# Revit family: AISC Tube Shapes-Section
name_source: partatom
category: Detail Items
revit_build: Autodesk Revit Architecture 2012 (Build: 20110210_1515)
units: mm (PartAtom-declared; Revit-internal decimal feet)

## types (374) — shared parameters
Keynote = 05 12 00.L0

## per-type parameters (varying)
| type | A | Ht | Shape | W | b | r | t |
| HSS20X12X5/8 | 0.24 SF | 1' - 8" | Rect. | 127 | 1' - 0" | 0' - 1 5/32" | 0' - 0 19/32" |
| HSS20X12X1/2 | 0.2 SF | 1' - 8" | Rect. | 103 | 1' - 0" | 0' - 0 15/16" | 0' - 0 15/32" |
| HSS20X12X3/8 | 0.15 SF | 1' - 8" | Rect. | 78.4 | 1' - 0" | 0' - 0 11/16" | 0' - 0 11/32" |
| HSS20X12X5/16 | 0.13 SF | 1' - 8" | Rect. | 65.8 | 1' - 0" | 0' - 0 19/32" | 0' - 0 9/32" |
| HSS20X8X5/8 | 0.21 SF | 1' - 8" | Rect. | 110 | 0' - 8" | 0' - 1 5/32" | 0' - 0 19/32" |
| HSS20X8X1/2 | 0.17 SF | 1' - 8" | Rect. | 89.6 | 0' - 8" | 0' - 0 15/16" | 0' - 0 15/32" |
| HSS20X8X3/8 | 0.13 SF | 1' - 8" | Rect. | 68.3 | 0' - 8" | 0' - 0 11/16" | 0' - 0 11/32" |
| HSS20X8X5/16 | 0.11 SF | 1' - 8" | Rect. | 57.3 | 0' - 8" | 0' - 0 19/32" | 0' - 0 9/32" |
| HSS20X4X1/2 | 0.15 SF | 1' - 8" | Rect. | 75.9 | 0' - 4" | 0' - 0 15/16" | 0' - 0 15/32" |
| HSS20X4X3/8 | 0.11 SF | 1' - 8" | Rect. | 58.1 | 0' - 4" | 0' - 0 11/16" | 0' - 0 11/32" |
| HSS20X4X5/16 | 0.09 SF | 1' - 8" | Rect. | 48.9 | 0' - 4" | 0' - 0 19/32" | 0' - 0 9/32" |
| HSS20X4X1/4 | 0.08 SF | 1' - 8" | Rect. | 39.5 | 0' - 4" | 0' - 0 15/32" | 0' - 0 7/32" |
| HSS18X12X5/8 - Obsolete | 0.23 SF | 1' - 6" | Rect. | 119 | 1' - 0" | 0' - 1 5/32" | 0' - 0 19/32" |
| HSS18X12X1/2 - Obsolete | 0.18 SF | 1' - 6" | Rect. | 96.4 | 1' - 0" | 0' - 0 15/16" | 0' - 0 15/32" |
| HSS18X12X3/8 - Obsolete | 0.14 SF | 1' - 6" | Rect. | 73.3 | 1' - 0" | 0' - 0 11/16" | 0' - 0 11/32" |
| HSS18X6X5/8 | 0.18 SF | 1' - 6" | Rect. | 93.1 | 0' - 6" | 0' - 1 5/32" | 0' - 0 19/32" |
| HSS18X6X1/2 | 0.15 SF | 1' - 6" | Rect. | 75.9 | 0' - 6" | 0' - 0 15/16" | 0' - 0 15/32" |
| HSS18X6X3/8 | 0.11 SF | 1' - 6" | Rect. | 58.1 | 0' - 6" | 0' - 0 11/16" | 0' - 0 11/32" |
| HSS18X6X5/16 | 0.09 SF | 1' - 6" | Rect. | 48.9 | 0' - 6" | 0' - 0 19/32" | 0' - 0 9/32" |
| HSS18X6X1/4 | 0.08 SF | 1' - 6" | Rect. | 39.5 | 0' - 6" | 0' - 0 15/32" | 0' - 0 7/32" |
| HSS16X16X5/8 | 0.24 SF | 1' - 4" | Square | 127 | 1' - 4" | 0' - 1 5/32" | 0' - 0 19/32" |
| HSS16X16X1/2 | 0.2 SF | 1' - 4" | Square | 103 | 1' - 4" | 0' - 0 15/16" | 0' - 0 15/32" |
| HSS16X16X3/8 | 0.15 SF | 1' - 4" | Square | 78.4 | 1' - 4" | 0' - 0 11/16" | 0' - 0 11/32" |
| HSS16X16X5/16 | 0.13 SF | 1' - 4" | Square | 65.8 | 1' - 4" | 0' - 0 19/32" | 0' - 0 9/32" |
| HSS16X12X5/8 | 0.21 SF | 1' - 4" | Rect. | 110 | 1' - 0" | 0' - 1 5/32" | 0' - 0 19/32" |
| HSS16X12X1/2 | 0.17 SF | 1' - 4" | Rect. | 89.6 | 1' - 0" | 0' - 0 15/16" | 0' - 0 15/32" |
| HSS16X12X3/8 | 0.13 SF | 1' - 4" | Rect. | 68.3 | 1' - 0" | 0' - 0 11/16" | 0' - 0 11/32" |
| HSS16X12X5/16 | 0.11 SF | 1' - 4" | Rect. | 57.4 | 1' - 0" | 0' - 0 19/32" | 0' - 0 9/32" |
| HSS16X8X5/8 | 0.18 SF | 1' - 4" | Rect. | 93.1 | 0' - 8" | 0' - 1 5/32" | 0' - 0 19/32" |
| HSS16X8X1/2 | 0.15 SF | 1' - 4" | Rect. | 75.9 | 0' - 8" | 0' - 0 15/16" | 0' - 0 15/32" |
| HSS16X8X3/8 | 0.11 SF | 1' - 4" | Rect. | 58.1 | 0' - 8" | 0' - 0 11/16" | 0' - 0 11/32" |
| HSS16X8X5/16 | 0.09 SF | 1' - 4" | Rect. | 48.9 | 0' - 8" | 0' - 0 19/32" | 0' - 0 9/32" |
| HSS16X8X1/4 | 0.08 SF | 1' - 4" | Rect. | 39.5 | 0' - 8" | 0' - 0 15/32" | 0' - 0 7/32" |
| HSS16X4X5/8 | 0.15 SF | 1' - 4" | Rect. | 76.1 | 0' - 4" | 0' - 1 5/32" | 0' - 0 19/32" |
| HSS16X4X1/2 | 0.12 SF | 1' - 4" | Rect. | 62.3 | 0' - 4" | 0' - 0 15/16" | 0' - 0 15/32" |
| HSS16X4X3/8 | 0.09 SF | 1' - 4" | Rect. | 47.9 | 0' - 4" | 0' - 0 11/16" | 0' - 0 11/32" |
| HSS16X4X5/16 | 0.08 SF | 1' - 4" | Rect. | 40.3 | 0' - 4" | 0' - 0 19/32" | 0' - 0 9/32" |
| HSS16X4X1/4 | 0.06 SF | 1' - 4" | Rect. | 32.7 | 0' - 4" | 0' - 0 15/32" | 0' - 0 7/32" |
| HSS16X4X3/16 | 0.05 SF | 1' - 2" | Rect. | 24.7 | 0' - 4" | 0' - 0 11/32" | 0' - 0 3/16" |
| HSS14X14X5/8 | 0.21 SF | 1' - 2" | Square | 110 | 1' - 2" | 0' - 1 5/32" | 0' - 0 19/32" |
| HSS14X14X1/2 | 0.17 SF | 1' - 2" | Square | 89.6 | 1' - 2" | 0' - 0 15/16" | 0' - 0 15/32" |
| HSS14X14X3/8 | 0.13 SF | 1' - 2" | Square | 68.2 | 1' - 2" | 0' - 0 11/16" | 0' - 0 11/32" |
| HSS14X14X5/16 | 0.11 SF | 1' - 2" | Square | 57.3 | 1' - 2" | 0' - 0 19/32" | 0' - 0 9/32" |
| HSS14X12X1/2 - Obsolete | 0.16 SF | 1' - 2" | Rect. | 82.7 | 1' - 0" | 0' - 0 15/16" | 0' - 0 15/32" |
| HSS14X12X3/8 - Obsolete | 0.12 SF | 1' - 2" | Rect. | 63.1 | 1' - 0" | 0' - 0 11/16" | 0' - 0 11/32" |
| HSS14X10X5/8 | 0.18 SF | 1' - 2" | Rect. | 93.1 | 0' - 10" | 0' - 1 5/32" | 0' - 0 19/32" |
| HSS14X10X1/2 | 0.15 SF | 1' - 2" | Rect. | 75.9 | 0' - 10" | 0' - 0 15/16" | 0' - 0 15/32" |
| HSS14X10X3/8 | 0.11 SF | 1' - 2" | Rect. | 58.1 | 0' - 10" | 0' - 0 11/16" | 0' - 0 11/32" |
| HSS14X10X5/16 | 0.09 SF | 1' - 2" | Rect. | 48.9 | 0' - 10" | 0' - 0 19/32" | 0' - 0 9/32" |
| HSS14X10X1/4 | 0.08 SF | 1' - 2" | Rect. | 39.5 | 0' - 10" | 0' - 0 15/32" | 0' - 0 7/32" |
| HSS14X6X5/8 | 0.15 SF | 1' - 2" | Rect. | 76.1 | 0' - 10" | 0' - 1 5/32" | 0' - 0 19/32" |
| HSS14X6X1/2 | 0.12 SF | 1' - 2" | Rect. | 62.3 | 0' - 6" | 0' - 0 15/16" | 0' - 0 15/32" |
| HSS14X6X3/8 | 0.09 SF | 1' - 2" | Rect. | 47.9 | 0' - 6" | 0' - 0 11/16" | 0' - 0 11/32" |
| HSS14X6X5/16 | 0.08 SF | 1' - 2" | Rect. | 40.3 | 0' - 6" | 0' - 0 19/32" | 0' - 0 9/32" |
| HSS14X6X1/4 | 0.06 SF | 1' - 2" | Rect. | 32.7 | 0' - 6" | 0' - 0 15/32" | 0' - 0 7/32" |
| HSS14X6X3/16 | 0.05 SF | 1' - 2" | Rect. | 24.7 | 0' - 6" | 0' - 0 11/32" | 0' - 0 3/16" |
| HSS14X4X5/8 | 0.13 SF | 1' - 2" | Rect. | 67.6 | 0' - 4" | 0' - 1 5/32" | 0' - 0 19/32" |
| HSS14X4X1/2 | 0.11 SF | 1' - 2" | Rect. | 55.5 | 0' - 4" | 0' - 0 15/16" | 0' - 0 15/32" |
| HSS14X4X3/8 | 0.08 SF | 1' - 2" | Rect. | 42.7 | 0' - 4" | 0' - 0 11/16" | 0' - 0 11/32" |
| HSS14X4X5/16 | 0.07 SF | 1' - 2" | Rect. | 36.1 | 0' - 4" | 0' - 0 19/32" | 0' - 0 9/32" |
| HSS14X4X1/4 | 0.06 SF | 1' - 2" | Rect. | 29.2 | 0' - 4" | 0' - 0 15/32" | 0' - 0 7/32" |
| HSS14X4X3/16 | 0.04 SF | 1' - 2" | Rect. | 22.1 | 0' - 4" | 0' - 0 11/32" | 0' - 0 3/16" |
| HSS12X12X5/8 | 0.18 SF | 1' - 0" | Square | 93.1 | 1' - 0" | 0' - 1 5/32" | 0' - 0 19/32" |
| HSS12X12X1/2 | 0.15 SF | 1' - 0" | Square | 75.9 | 1' - 0" | 0' - 0 15/16" | 0' - 0 15/32" |
| HSS12X12X3/8 | 0.11 SF | 1' - 0" | Square | 58 | 1' - 0" | 0' - 0 11/16" | 0' - 0 11/32" |
| HSS12X12X5/16 | 0.09 SF | 1' - 0" | Square | 48.8 | 1' - 0" | 0' - 0 19/32" | 0' - 0 9/32" |
| HSS12X12X1/4 | 0.08 SF | 1' - 0" | Square | 39.4 | 1' - 0" | 0' - 0 15/32" | 0' - 0 7/32" |
| HSS12X12X3/16 | 0.06 SF | 1' - 0" | Square | 29.8 | 1' - 0" | 0' - 0 11/32" | 0' - 0 3/16" |
| HSS12X10X1/2 | 0.13 SF | 1' - 0" | Rect. | 69.1 | 0' - 10" | 0' - 0 15/16" | 0' - 0 15/32" |
| HSS12X10X3/8 | 0.1 SF | 1' - 0" | Rect. | 52.9 | 0' - 10" | 0' - 0 11/16" | 0' - 0 11/32" |
| HSS12X10X5/16 | 0.08 SF | 1' - 0" | Rect. | 44.6 | 0' - 10" | 0' - 0 19/32" | 0' - 0 9/32" |
| HSS12X10X1/4 | 0.07 SF | 1' - 0" | Rect. | 36 | 0' - 10" | 0' - 0 15/32" | 0' - 0 7/32" |
| HSS12X8X5/8 | 0.15 SF | 1' - 0" | Rect. | 76.1 | 0' - 8" | 0' - 1 5/32" | 0' - 0 19/32" |
| HSS12X8X1/2 | 0.12 SF | 1' - 0" | Rect. | 62.3 | 0' - 8" | 0' - 0 15/16" | 0' - 0 15/32" |
| HSS12X8X3/8 | 0.09 SF | 1' - 0" | Rect. | 47.8 | 0' - 8" | 0' - 0 11/16" | 0' - 0 11/32" |
| HSS12X8X5/16 | 0.08 SF | 1' - 0" | Rect. | 40.4 | 0' - 8" | 0' - 0 19/32" | 0' - 0 9/32" |
| HSS12X8X1/4 | 0.06 SF | 1' - 0" | Rect. | 32.6 | 0' - 8" | 0' - 0 15/32" | 0' - 0 7/32" |
| HSS12X8X3/16 | 0.05 SF | 1' - 0" | Rect. | 24.8 | 0' - 8" | 0' - 0 11/32" | 0' - 0 3/16" |
| HSS12X6X5/8 | 0.13 SF | 1' - 0" | Rect. | 67.6 | 0' - 6" | 0' - 1 5/32" | 0' - 0 19/32" |
| HSS12X6X1/2 | 0.11 SF | 1' - 0" | Rect. | 55.5 | 0' - 6" | 0' - 0 15/16" | 0' - 0 15/32" |
| HSS12X6X3/8 | 0.08 SF | 1' - 0" | Rect. | 42.7 | 0' - 6" | 0' - 0 11/16" | 0' - 0 11/32" |
| HSS12X6X5/16 | 0.07 SF | 1' - 0" | Rect. | 36.1 | 0' - 6" | 0' - 0 19/32" | 0' - 0 9/32" |
| HSS12X6X1/4 | 0.06 SF | 1' - 0" | Rect. | 29.2 | 0' - 6" | 0' - 0 15/32" | 0' - 0 7/32" |
| HSS12X6X3/16 | 0.04 SF | 1' - 0" | Rect. | 22.2 | 0' - 6" | 0' - 0 11/32" | 0' - 0 3/16" |
| HSS12X4X5/8 | 0.11 SF | 1' - 0" | Rect. | 59.1 | 0' - 4" | 0' - 1 5/32" | 0' - 0 19/32" |
| HSS12X4X1/2 | 0.09 SF | 1' - 0" | Rect. | 48.7 | 0' - 4" | 0' - 0 15/16" | 0' - 0 15/32" |
| HSS12X4X3/8 | 0.07 SF | 1' - 0" | Rect. | 37.6 | 0' - 4" | 0' - 0 11/16" | 0' - 0 11/32" |
| HSS12X4X5/16 | 0.06 SF | 1' - 0" | Rect. | 31.8 | 0' - 4" | 0' - 0 19/32" | 0' - 0 9/32" |
| HSS12X4X1/4 | 0.05 SF | 1' - 0" | Rect. | 25.8 | 0' - 4" | 0' - 0 15/32" | 0' - 0 7/32" |
| HSS12X4X3/16 | 0.04 SF | 1' - 0" | Rect. | 19.7 | 0' - 4" | 0' - 0 11/32" | 0' - 0 3/16" |
| HSS12X3-1/2X3/8 | 0.07 SF | 1' - 0" | Rect. | 36.3 | 0' - 3 1/2" | 0' - 0 11/16" | 0' - 0 11/32" |
| HSS12X3-1/2X5/16 | 0.06 SF | 1' - 0" | Rect. | 30.8 | 0' - 3 1/2" | 0' - 0 19/32" | 0' - 0 9/32" |
| HSS12X3X5/16 | 0.06 SF | 1' - 0" | Rect. | 29.7 | 0' - 3" | 0' - 0 19/32" | 0' - 0 9/32" |
| HSS12X3X1/4 | 0.05 SF | 1' - 0" | Rect. | 24.1 | 0' - 3" | 0' - 0 15/32" | 0' - 0 7/32" |
| HSS12X3X3/16 | 0.03 SF | 1' - 0" | Rect. | 18.4 | 0' - 3" | 0' - 0 11/32" | 0' - 0 3/16" |
| HSS12X2X5/16 | 0.05 SF | 1' - 0" | Rect. | 27.6 | 0' - 2" | 0' - 0 19/32" | 0' - 0 9/32" |
| HSS12X2X1/4 | 0.04 SF | 1' - 0" | Rect. | 22.4 | 0' - 2" | 0' - 0 15/32" | 0' - 0 7/32" |
| HSS12X2X3/16 | 0.03 SF | 1' - 0" | Rect. | 17.1 | 0' - 2" | 0' - 0 11/32" | 0' - 0 3/16" |
| HSS10X10X5/8 | 0.15 SF | 0' - 10" | Square | 76.1 | 0' - 10" | 0' - 1 5/32" | 0' - 0 19/32" |
| HSS10X10X1/2 | 0.12 SF | 0' - 10" | Square | 62.3 | 0' - 10" | 0' - 0 15/16" | 0' - 0 15/32" |
| HSS10X10X3/8 | 0.09 SF | 0' - 10" | Square | 47.8 | 0' - 10" | 0' - 0 11/16" | 0' - 0 11/32" |
| HSS10X10X5/16 | 0.08 SF | 0' - 10" | Square | 40.3 | 0' - 10" | 0' - 0 19/32" | 0' - 0 9/32" |
| HSS10X10X1/4 | 0.06 SF | 0' - 10" | Square | 32.6 | 0' - 10" | 0' - 0 15/32" | 0' - 0 7/32" |
| HSS10X10X3/16 | 0.05 SF | 0' - 10" | Square | 24.7 | 0' - 10" | 0' - 0 11/32" | 0' - 0 3/16" |
| HSS10X8X5/8 | 0.13 SF | 0' - 10" | Rect. | 67.6 | 0' - 8" | 0' - 1 5/32" | 0' - 0 19/32" |
| HSS10X8X1/2 | 0.11 SF | 0' - 10" | Rect. | 55.5 | 0' - 8" | 0' - 0 15/16" | 0' - 0 15/32" |
| HSS10X8X3/8 | 0.08 SF | 0' - 10" | Rect. | 42.7 | 0' - 8" | 0' - 0 11/16" | 0' - 0 11/32" |
| HSS10X8X5/16 | 0.07 SF | 0' - 10" | Rect. | 36.1 | 0' - 8" | 0' - 0 19/32" | 0' - 0 9/32" |
| HSS10X8X1/4 | 0.06 SF | 0' - 10" | Rect. | 29.2 | 0' - 8" | 0' - 0 15/32" | 0' - 0 7/32" |
| HSS10X8X3/16 | 0.04 SF | 0' - 10" | Rect. | 22.2 | 0' - 8" | 0' - 0 11/32" | 0' - 0 3/16" |
| HSS10X6X5/8 | 0.11 SF | 0' - 10" | Rect. | 59.1 | 0' - 6" | 0' - 1 5/32" | 0' - 0 19/32" |
| HSS10X6X1/2 | 0.09 SF | 0' - 10" | Rect. | 48.7 | 0' - 6" | 0' - 0 15/16" | 0' - 0 15/32" |
| HSS10X6X3/8 | 0.07 SF | 0' - 10" | Rect. | 37.6 | 0' - 6" | 0' - 0 11/16" | 0' - 0 11/32" |
| HSS10X6X5/16 | 0.06 SF | 0' - 10" | Rect. | 31.8 | 0' - 6" | 0' - 0 19/32" | 0' - 0 9/32" |
| HSS10X6X1/4 | 0.05 SF | 0' - 10" | Rect. | 25.8 | 0' - 6" | 0' - 0 15/32" | 0' - 0 7/32" |
| HSS10X6X3/16 | 0.04 SF | 0' - 10" | Rect. | 19.7 | 0' - 6" | 0' - 0 11/32" | 0' - 0 3/16" |
| HSS10X5X3/8 | 0.07 SF | 0' - 10" | Rect. | 35.1 | 0' - 5" | 0' - 0 11/16" | 0' - 0 11/32" |
| HSS10X5X5/16 | 0.06 SF | 0' - 10" | Rect. | 29.7 | 0' - 5" | 0' - 0 19/32" | 0' - 0 9/32" |
| HSS10X5X1/4 | 0.05 SF | 0' - 10" | Rect. | 24.1 | 0' - 5" | 0' - 0 15/32" | 0' - 0 7/32" |
| HSS10X5X3/16 | 0.03 SF | 0' - 10" | Rect. | 18.4 | 0' - 5" | 0' - 0 11/32" | 0' - 0 3/16" |
| HSS10X4X5/8 | 0.1 SF | 0' - 10" | Rect. | 50.6 | 0' - 4" | 0' - 1 5/32" | 0' - 0 19/32" |
| HSS10X4X1/2 | 0.08 SF | 0' - 10" | Rect. | 41.9 | 0' - 4" | 0' - 0 15/16" | 0' - 0 15/32" |
| HSS10X4X3/8 | 0.06 SF | 0' - 10" | Rect. | 32.5 | 0' - 4" | 0' - 0 11/16" | 0' - 0 11/32" |
| HSS10X4X5/16 | 0.05 SF | 0' - 10" | Rect. | 27.6 | 0' - 4" | 0' - 0 19/32" | 0' - 0 9/32" |
| HSS10X4X1/4 | 0.04 SF | 0' - 10" | Rect. | 22.4 | 0' - 4" | 0' - 0 15/32" | 0' - 0 7/32" |
| HSS10X4X3/16 | 0.03 SF | 0' - 10" | Rect. | 17.1 | 0' - 4" | 0' - 0 11/32" | 0' - 0 3/16" |
| HSS10X4X1/8 | 0.02 SF | 0' - 10" | Rect. | 11.6 | 0' - 4" | 0' - 0 7/32" | 0' - 0 1/8" |
| HSS10X3-1/2X1/2 | 0.08 SF | 0' - 10" | Rect. | 40.2 | 0' - 3 1/2" | 0' - 0 15/16" | 0' - 0 15/32" |
| HSS10X3-1/2X3/8 | 0.06 SF | 0' - 10" | Rect. | 31.2 | 0' - 3 1/2" | 0' - 0 11/16" | 0' - 0 11/32" |
| HSS10X3-1/2X5/16 | 0.05 SF | 0' - 10" | Rect. | 26.5 | 0' - 3 1/2" | 0' - 0 19/32" | 0' - 0 9/32" |
| HSS10X3-1/2X1/4 | 0.04 SF | 0' - 10" | Rect. | 21.5 | 0' - 3 1/2" | 0' - 0 15/32" | 0' - 0 7/32" |
| HSS10X3-1/2X3/16 | 0.03 SF | 0' - 10" | Rect. | 16.5 | 0' - 3 1/2" | 0' - 0 11/32" | 0' - 0 3/16" |
| HSS10X3-1/2X1/8 | 0.02 SF | 0' - 10" | Rect. | 11.1 | 0' - 3 1/2" | 0' - 0 7/32" | 0' - 0 1/8" |
| HSS10X3X3/8 | 0.06 SF | 0' - 10" | Rect. | 30 | 0' - 3" | 0' - 0 11/16" | 0' - 0 11/32" |
| HSS10X3X5/16 | 0.05 SF | 0' - 10" | Rect. | 25.4 | 0' - 3" | 0' - 0 19/32" | 0' - 0 9/32" |
| HSS10X3X1/4 | 0.04 SF | 0' - 10" | Rect. | 20.7 | 0' - 3" | 0' - 0 15/32" | 0' - 0 7/32" |
| HSS10X3X3/16 | 0.03 SF | 0' - 10" | Rect. | 15.8 | 0' - 3" | 0' - 0 11/32" | 0' - 0 3/16" |
| HSS10X3X1/8 | 0.02 SF | 0' - 10" | Rect. | 10.7 | 0' - 3" | 0' - 0 7/32" | 0' - 0 1/8" |
| HSS10X2X3/8 | 0.05 SF | 0' - 10" | Rect. | 27.4 | 0' - 2" | 0' - 0 11/16" | 0' - 0 11/32" |
| HSS10X2X5/16 | 0.04 SF | 0' - 10" | Rect. | 23.3 | 0' - 2" | 0' - 0 19/32" | 0' - 0 9/32" |
| HSS10X2X1/4 | 0.04 SF | 0' - 10" | Rect. | 19 | 0' - 2" | 0' - 0 15/32" | 0' - 0 7/32" |
| HSS10X2X3/16 | 0.03 SF | 0' - 10" | Rect. | 14.5 | 0' - 2" | 0' - 0 11/32" | 0' - 0 3/16" |
| HSS10X2X1/8 | 0.02 SF | 0' - 10" | Rect. | 9.85 | 0' - 2" | 0' - 0 7/32" | 0' - 0 1/8" |
| HSS9X9X5/8 | 0.13 SF | 0' - 9" | Square | 67.6 | 0' - 9" | 0' - 1 5/32" | 0' - 0 19/32" |
| HSS9X9X1/2 | 0.11 SF | 0' - 9" | Square | 55.5 | 0' - 9" | 0' - 0 15/16" | 0' - 0 15/32" |
| HSS9X9X3/8 | 0.08 SF | 0' - 9" | Square | 42.7 | 0' - 9" | 0' - 0 11/16" | 0' - 0 11/32" |
| HSS9X9X5/16 | 0.07 SF | 0' - 9" | Square | 36 | 0' - 9" | 0' - 0 19/32" | 0' - 0 9/32" |
| HSS9X9X1/4 | 0.06 SF | 0' - 9" | Square | 29.2 | 0' - 9" | 0' - 0 15/32" | 0' - 0 7/32" |
| HSS9X9X3/16 | 0.04 SF | 0' - 9" | Square | 22.2 | 0' - 9" | 0' - 0 11/32" | 0' - 0 3/16" |
| HSS9X9X1/8 | 0.03 SF | 0' - 9" | Square | 15 | 0' - 9" | 0' - 0 7/32" | 0' - 0 1/8" |
| HSS9X7X5/8 | 0.11 SF | 0' - 9" | Rect. | 59.1 | 0' - 7" | 0' - 1 5/32" | 0' - 0 19/32" |
| HSS9X7X1/2 | 0.09 SF | 0' - 9" | Rect. | 48.7 | 0' - 7" | 0' - 0 15/16" | 0' - 0 15/32" |
| HSS9X7X3/8 | 0.07 SF | 0' - 9" | Rect. | 37.6 | 0' - 7" | 0' - 0 11/16" | 0' - 0 11/32" |
| HSS9X7X5/16 | 0.06 SF | 0' - 9" | Rect. | 31.8 | 0' - 7" | 0' - 0 19/32" | 0' - 0 9/32" |
| HSS9X7X1/4 | 0.05 SF | 0' - 9" | Rect. | 25.8 | 0' - 7" | 0' - 0 15/32" | 0' - 0 7/32" |
| HSS9X7X3/16 | 0.04 SF | 0' - 9" | Rect. | 19.7 | 0' - 7" | 0' - 0 11/32" | 0' - 0 3/16" |
| HSS9X5X5/8 | 0.1 SF | 0' - 9" | Rect. | 50.6 | 0' - 5" | 0' - 1 5/32" | 0' - 0 19/32" |
| HSS9X5X1/2 | 0.08 SF | 0' - 9" | Rect. | 41.9 | 0' - 5" | 0' - 0 15/16" | 0' - 0 15/32" |
| HSS9X5X3/8 | 0.06 SF | 0' - 9" | Rect. | 32.5 | 0' - 5" | 0' - 0 11/16" | 0' - 0 11/32" |
| HSS9X5X5/16 | 0.05 SF | 0' - 9" | Rect. | 27.6 | 0' - 5" | 0' - 0 19/32" | 0' - 0 9/32" |
| HSS9X5X1/4 | 0.04 SF | 0' - 9" | Rect. | 22.4 | 0' - 5" | 0' - 0 15/32" | 0' - 0 7/32" |
| HSS9X5X3/16 | 0.03 SF | 0' - 9" | Rect. | 17.1 | 0' - 5" | 0' - 0 11/32" | 0' - 0 3/16" |
| HSS9X3X1/2 | 0.07 SF | 0' - 9" | Rect. | 35.1 | 0' - 3" | 0' - 0 15/16" | 0' - 0 15/32" |
| HSS9X3X3/8 | 0.05 SF | 0' - 9" | Rect. | 27.4 | 0' - 3" | 0' - 0 11/16" | 0' - 0 11/32" |
| HSS9X3X5/16 | 0.04 SF | 0' - 9" | Rect. | 23.3 | 0' - 3" | 0' - 0 19/32" | 0' - 0 9/32" |
| HSS9X3X1/4 | 0.04 SF | 0' - 9" | Rect. | 19 | 0' - 3" | 0' - 0 15/32" | 0' - 0 7/32" |
| HSS9X3X3/16 | 0.03 SF | 0' - 9" | Rect. | 14.5 | 0' - 3" | 0' - 0 11/32" | 0' - 0 3/16" |
| HSS8X8X5/8 | 0.11 SF | 0' - 8" | Square | 59.1 | 0' - 8" | 0' - 1 5/32" | 0' - 0 19/32" |
| HSS8X8X1/2 | 0.09 SF | 0' - 8" | Square | 48.7 | 0' - 8" | 0' - 0 15/16" | 0' - 0 15/32" |
| HSS8X8X3/8 | 0.07 SF | 0' - 8" | Square | 37.6 | 0' - 8" | 0' - 0 11/16" | 0' - 0 11/32" |
| HSS8X8X5/16 | 0.06 SF | 0' - 8" | Square | 31.8 | 0' - 8" | 0' - 0 19/32" | 0' - 0 9/32" |
| HSS8X8X1/4 | 0.05 SF | 0' - 8" | Square | 25.8 | 0' - 8" | 0' - 0 15/32" | 0' - 0 7/32" |
| HSS8X8X3/16 | 0.04 SF | 0' - 8" | Square | 19.6 | 0' - 8" | 0' - 0 11/32" | 0' - 0 3/16" |
| HSS8X8X1/8 | 0.03 SF | 0' - 8" | Square | 13.3 | 0' - 8" | 0' - 0 7/32" | 0' - 0 1/8" |
| HSS8X6X5/8 | 0.1 SF | 0' - 8" | Rect. | 50.6 | 0' - 6" | 0' - 1 5/32" | 0' - 0 19/32" |
| HSS8X6X1/2 | 0.08 SF | 0' - 8" | Rect. | 41.9 | 0' - 6" | 0' - 0 15/16" | 0' - 0 15/32" |
| HSS8X6X3/8 | 0.06 SF | 0' - 8" | Rect. | 32.5 | 0' - 6" | 0' - 0 11/16" | 0' - 0 11/32" |
| HSS8X6X5/16 | 0.05 SF | 0' - 8" | Rect. | 27.6 | 0' - 6" | 0' - 0 19/32" | 0' - 0 9/32" |
| HSS8X6X1/4 | 0.04 SF | 0' - 8" | Rect. | 22.4 | 0' - 6" | 0' - 0 15/32" | 0' - 0 7/32" |
| HSS8X6X3/16 | 0.03 SF | 0' - 8" | Rect. | 17.1 | 0' - 6" | 0' - 0 11/32" | 0' - 0 3/16" |
| HSS8X4X5/8 | 0.08 SF | 0' - 8" | Rect. | 42.1 | 0' - 4" | 0' - 1 5/32" | 0' - 0 19/32" |
| HSS8X4X1/2 | 0.07 SF | 0' - 8" | Rect. | 35.1 | 0' - 4" | 0' - 0 15/16" | 0' - 0 15/32" |
| HSS8X4X3/8 | 0.05 SF | 0' - 8" | Rect. | 27.4 | 0' - 4" | 0' - 0 11/16" | 0' - 0 11/32" |
| HSS8X4X5/16 | 0.04 SF | 0' - 8" | Rect. | 23.3 | 0' - 4" | 0' - 0 19/32" | 0' - 0 9/32" |
| HSS8X4X1/4 | 0.04 SF | 0' - 8" | Rect. | 19 | 0' - 4" | 0' - 0 15/32" | 0' - 0 7/32" |
| HSS8X4X3/16 | 0.03 SF | 0' - 8" | Rect. | 14.5 | 0' - 4" | 0' - 0 11/32" | 0' - 0 3/16" |
| HSS8X4X1/8 | 0.02 SF | 0' - 8" | Rect. | 9.85 | 0' - 4" | 0' - 0 7/32" | 0' - 0 1/8" |
| HSS8X3X1/2 | 0.06 SF | 0' - 8" | Rect. | 31.7 | 0' - 3" | 0' - 0 15/16" | 0' - 0 15/32" |
| HSS8X3X3/8 | 0.05 SF | 0' - 8" | Rect. | 24.9 | 0' - 3" | 0' - 0 11/16" | 0' - 0 11/32" |
| HSS8X3X5/16 | 0.04 SF | 0' - 8" | Rect. | 21.2 | 0' - 3" | 0' - 0 19/32" | 0' - 0 9/32" |
| HSS8X3X1/4 | 0.03 SF | 0' - 8" | Rect. | 17.3 | 0' - 3" | 0' - 0 15/32" | 0' - 0 7/32" |
| HSS8X3X3/16 | 0.03 SF | 0' - 8" | Rect. | 13.3 | 0' - 3" | 0' - 0 11/32" | 0' - 0 3/16" |
| HSS8X3X1/8 | 0.02 SF | 0' - 8" | Rect. | 9 | 0' - 3" | 0' - 0 7/32" | 0' - 0 1/8" |
| HSS8X2X3/8 | 0.04 SF | 0' - 8" | Rect. | 22.3 | 0' - 2" | 0' - 0 11/16" | 0' - 0 11/32" |
| HSS8X2X5/16 | 0.04 SF | 0' - 8" | Rect. | 19.1 | 0' - 2" | 0' - 0 19/32" | 0' - 0 9/32" |
| HSS8X2X1/4 | 0.03 SF | 0' - 8" | Rect. | 15.6 | 0' - 2" | 0' - 0 15/32" | 0' - 0 7/32" |
| HSS8X2X3/16 | 0.02 SF | 0' - 8" | Rect. | 12 | 0' - 2" | 0' - 0 11/32" | 0' - 0 3/16" |
| HSS8X2X1/8 | 0.02 SF | 0' - 8" | Rect. | 8.15 | 0' - 2" | 0' - 0 7/32" | 0' - 0 1/8" |
| HSS7X7X5/8 | 0.1 SF | 0' - 7" | Square | 50.6 | 0' - 7" | 0' - 1 5/32" | 0' - 0 19/32" |
| HSS7X7X1/2 | 0.08 SF | 0' - 7" | Square | 41.9 | 0' - 7" | 0' - 0 15/16" | 0' - 0 15/32" |
| HSS7X7X3/8 | 0.06 SF | 0' - 7" | Square | 32.5 | 0' - 7" | 0' - 0 11/16" | 0' - 0 11/32" |
| HSS7X7X5/16 | 0.05 SF | 0' - 7" | Square | 27.5 | 0' - 7" | 0' - 0 19/32" | 0' - 0 9/32" |
| HSS7X7X1/4 | 0.04 SF | 0' - 7" | Square | 22.4 | 0' - 7" | 0' - 0 15/32" | 0' - 0 7/32" |
| HSS7X7X3/16 | 0.03 SF | 0' - 7" | Square | 17.1 | 0' - 7" | 0' - 0 11/32" | 0' - 0 3/16" |
| HSS7X7X1/8 | 0.02 SF | 0' - 7" | Square | 11.6 | 0' - 7" | 0' - 0 7/32" | 0' - 0 1/8" |
| HSS7X5X1/2 | 0.07 SF | 0' - 7" | Rect. | 35.1 | 0' - 5" | 0' - 0 15/16" | 0' - 0 15/32" |
| HSS7X5X3/8 | 0.05 SF | 0' - 7" | Rect. | 27.4 | 0' - 5" | 0' - 0 11/16" | 0' - 0 11/32" |
| HSS7X5X5/16 | 0.04 SF | 0' - 7" | Rect. | 23.3 | 0' - 5" | 0' - 0 19/32" | 0' - 0 9/32" |
| HSS7X5X1/4 | 0.04 SF | 0' - 7" | Rect. | 19 | 0' - 5" | 0' - 0 15/32" | 0' - 0 7/32" |
| HSS7X5X3/16 | 0.03 SF | 0' - 7" | Rect. | 14.5 | 0' - 5" | 0' - 0 11/32" | 0' - 0 3/16" |
| HSS7X5X1/8 | 0.02 SF | 0' - 7" | Rect. | 9.85 | 0' - 5" | 0' - 0 7/32" | 0' - 0 1/8" |
| HSS7X4X1/2 | 0.06 SF | 0' - 7" | Rect. | 31.7 | 0' - 4" | 0' - 0 15/16" | 0' - 0 15/32" |
| HSS7X4X3/8 | 0.05 SF | 0' - 7" | Rect. | 24.9 | 0' - 4" | 0' - 0 11/16" | 0' - 0 11/32" |
| HSS7X4X5/16 | 0.04 SF | 0' - 7" | Rect. | 21.2 | 0' - 4" | 0' - 0 19/32" | 0' - 0 9/32" |
| HSS7X4X1/4 | 0.03 SF | 0' - 7" | Rect. | 17.3 | 0' - 4" | 0' - 0 15/32" | 0' - 0 7/32" |
| HSS7X4X3/16 | 0.03 SF | 0' - 7" | Rect. | 13.3 | 0' - 4" | 0' - 0 11/32" | 0' - 0 3/16" |
| HSS7X4X1/8 | 0.02 SF | 0' - 7" | Rect. | 9 | 0' - 4" | 0' - 0 7/32" | 0' - 0 1/8" |
| HSS7X3X1/2 | 0.05 SF | 0' - 7" | Rect. | 28.3 | 0' - 3" | 0' - 0 15/16" | 0' - 0 15/32" |
| HSS7X3X3/8 | 0.04 SF | 0' - 7" | Rect. | 22.3 | 0' - 3" | 0' - 0 11/16" | 0' - 0 11/32" |
| HSS7X3X5/16 | 0.04 SF | 0' - 7" | Rect. | 19.1 | 0' - 3" | 0' - 0 19/32" | 0' - 0 9/32" |
| HSS7X3X1/4 | 0.03 SF | 0' - 7" | Rect. | 15.6 | 0' - 3" | 0' - 0 15/32" | 0' - 0 7/32" |
| HSS7X3X3/16 | 0.02 SF | 0' - 7" | Rect. | 12 | 0' - 3" | 0' - 0 11/32" | 0' - 0 3/16" |
| HSS7X3X1/8 | 0.02 SF | 0' - 7" | Rect. | 8.15 | 0' - 3" | 0' - 0 7/32" | 0' - 0 1/8" |
| HSS7X2X1/2 | 0.03 SF | 0' - 7" | Rect. | 13.9 | 0' - 2" | 0' - 0 15/32" | 0' - 0 7/32" |
| HSS7X2X3/16 | 0.02 SF | 0' - 7" | Rect. | 10.7 | 0' - 2" | 0' - 0 11/32" | 0' - 0 3/16" |
| HSS7X2X1/4 | 0.01 SF | 0' - 7" | Rect. | 7.3 | 0' - 2" | 0' - 0 7/32" | 0' - 0 1/8" |
| HSS6X6X5/8 | 0.08 SF | 0' - 6" | Square | 42.1 | 0' - 6" | 0' - 1 5/32" | 0' - 0 19/32" |
| HSS6X6X1/2 | 0.07 SF | 0' - 6" | Square | 35.1 | 0' - 6" | 0' - 0 15/16" | 0' - 0 15/32" |
| HSS6X6X3/8 | 0.05 SF | 0' - 6" | Square | 27.4 | 0' - 6" | 0' - 0 11/16" | 0' - 0 11/32" |
| HSS6X6X5/16 | 0.04 SF | 0' - 6" | Square | 23.3 | 0' - 6" | 0' - 0 19/32" | 0' - 0 9/32" |
| HSS6X6X1/4 | 0.04 SF | 0' - 6" | Square | 19 | 0' - 6" | 0' - 0 15/32" | 0' - 0 7/32" |
| HSS6X6X3/16 | 0.03 SF | 0' - 6" | Square | 14.5 | 0' - 6" | 0' - 0 11/32" | 0' - 0 3/16" |
| HSS6X6X1/8 | 0.02 SF | 0' - 6" | Square | 9.85 | 0' - 6" | 0' - 0 7/32" | 0' - 0 1/8" |
| HSS6X5X1/2 | 0.06 SF | 0' - 6" | Rect. | 31.7 | 0' - 5" | 0' - 0 15/16" | 0' - 0 15/32" |
| HSS6X5X3/8 | 0.05 SF | 0' - 6" | Rect. | 24.9 | 0' - 5" | 0' - 0 11/16" | 0' - 0 11/32" |
| HSS6X5X5/16 | 0.04 SF | 0' - 6" | Rect. | 21.2 | 0' - 5" | 0' - 0 19/32" | 0' - 0 9/32" |
| HSS6X5X1/4 | 0.03 SF | 0' - 6" | Rect. | 17.3 | 0' - 5" | 0' - 0 15/32" | 0' - 0 7/32" |
| HSS6X5X3/16 | 0.03 SF | 0' - 6" | Rect. | 13.3 | 0' - 5" | 0' - 0 11/32" | 0' - 0 3/16" |
| HSS6X5X1/8 | 0.02 SF | 0' - 6" | Rect. | 9 | 0' - 5" | 0' - 0 7/32" | 0' - 0 1/8" |
| HSS6X4X1/2 | 0.05 SF | 0' - 6" | Rect. | 28.3 | 0' - 4" | 0' - 0 15/16" | 0' - 0 15/32" |
| HSS6X4X3/8 | 0.04 SF | 0' - 6" | Rect. | 22.3 | 0' - 4" | 0' - 0 11/16" | 0' - 0 11/32" |
| HSS6X4X5/16 | 0.04 SF | 0' - 6" | Rect. | 19.1 | 0' - 4" | 0' - 0 19/32" | 0' - 0 9/32" |
| HSS6X4X1/4 | 0.03 SF | 0' - 6" | Rect. | 15.6 | 0' - 4" | 0' - 0 15/32" | 0' - 0 7/32" |
| HSS6X4X3/16 | 0.02 SF | 0' - 6" | Rect. | 12 | 0' - 4" | 0' - 0 11/32" | 0' - 0 3/16" |
| HSS6X4X1/8 | 0.02 SF | 0' - 6" | Rect. | 8.15 | 0' - 4" | 0' - 0 7/32" | 0' - 0 1/8" |
| HSS6X3X1/2 | 0.05 SF | 0' - 6" | Rect. | 24.9 | 0' - 3" | 0' - 0 15/16" | 0' - 0 15/32" |
| HSS6X3X3/8 | 0.04 SF | 0' - 6" | Rect. | 19.7 | 0' - 3" | 0' - 0 11/16" | 0' - 0 11/32" |
| HSS6X3X5/16 | 0.03 SF | 0' - 6" | Rect. | 16.9 | 0' - 3" | 0' - 0 19/32" | 0' - 0 9/32" |
| HSS6X3X1/4 | 0.03 SF | 0' - 6" | Rect. | 13.9 | 0' - 3" | 0' - 0 15/32" | 0' - 0 7/32" |
| HSS6X3X3/16 | 0.02 SF | 0' - 6" | Rect. | 10.7 | 0' - 3" | 0' - 0 11/32" | 0' - 0 3/16" |
| HSS6X3X1/8 | 0.01 SF | 0' - 6" | Rect. | 7.3 | 0' - 3" | 0' - 0 7/32" | 0' - 0 1/8" |
| HSS6X2X3/8 | 0.03 SF | 0' - 6" | Rect. | 17.2 | 0' - 2" | 0' - 0 11/16" | 0' - 0 11/32" |
| HSS6X2X5/16 | 0.03 SF | 0' - 6" | Rect. | 14.8 | 0' - 2" | 0' - 0 19/32" | 0' - 0 9/32" |
| HSS6X2X1/4 | 0.02 SF | 0' - 6" | Rect. | 12.2 | 0' - 2" | 0' - 0 15/32" | 0' - 0 7/32" |
| HSS6X2X3/16 | 0.02 SF | 0' - 6" | Rect. | 9.43 | 0' - 2" | 0' - 0 11/32" | 0' - 0 3/16" |
| HSS6X2X1/8 | 0.01 SF | 0' - 6" | Rect. | 6.45 | 0' - 2" | 0' - 0 7/32" | 0' - 0 1/8" |
| HSS5-1/2X5-1/2X3/8 | 0.05 SF | 0' - 5 1/2" | Square | 24.9 | 0' - 5 1/2" | 0' - 0 11/16" | 0' - 0 11/32" |
| HSS5-1/2X5-1/2X5/16 | 0.04 SF | 0' - 5 1/2" | Square | 21.2 | 0' - 5 1/2" | 0' - 0 19/32" | 0' - 0 9/32" |
| HSS5-1/2X5-1/2X1/4 | 0.03 SF | 0' - 5 1/2" | Square | 17.3 | 0' - 5 1/2" | 0' - 0 15/32" | 0' - 0 7/32" |
| HSS5-1/2X5-1/2X3/16 | 0.03 SF | 0' - 5 1/2" | Square | 13.2 | 0' - 5 1/2" | 0' - 0 11/32" | 0' - 0 3/16" |
| HSS5-1/2X5-1/2X1/8 | 0.02 SF | 0' - 5 1/2" | Square | 9 | 0' - 5 1/2" | 0' - 0 7/32" | 0' - 0 1/8" |
| HSS5X5X1/2 | 0.05 SF | 0' - 5" | Square | 28.3 | 0' - 5" | 0' - 0 15/16" | 0' - 0 15/32" |
| HSS5X5X3/8 | 0.04 SF | 0' - 5" | Square | 22.3 | 0' - 5" | 0' - 0 11/16" | 0' - 0 11/32" |
| HSS5X5X5/16 | 0.04 SF | 0' - 5" | Square | 19 | 0' - 5" | 0' - 0 19/32" | 0' - 0 9/32" |
| HSS5X5X1/4 | 0.03 SF | 0' - 5" | Square | 15.6 | 0' - 5" | 0' - 0 15/32" | 0' - 0 7/32" |
| HSS5X5X3/16 | 0.02 SF | 0' - 5" | Square | 12 | 0' - 5" | 0' - 0 11/32" | 0' - 0 3/16" |
| HSS5X5X1/8 | 0.02 SF | 0' - 5" | Square | 8.15 | 0' - 5" | 0' - 0 7/32" | 0' - 0 1/8" |
| HSS5X4X1/2 | 0.05 SF | 0' - 5" | Rect. | 24.9 | 0' - 4" | 0' - 0 15/16" | 0' - 0 15/32" |
| HSS5X4X3/8 | 0.04 SF | 0' - 5" | Rect. | 19.7 | 0' - 4" | 0' - 0 11/16" | 0' - 0 11/32" |
| HSS5X4X5/16 | 0.03 SF | 0' - 5" | Rect. | 16.9 | 0' - 4" | 0' - 0 19/32" | 0' - 0 9/32" |
| HSS5X4X1/4 | 0.03 SF | 0' - 5" | Rect. | 13.9 | 0' - 4" | 0' - 0 15/32" | 0' - 0 7/32" |
| HSS5X4X3/16 | 0.02 SF | 0' - 5" | Rect. | 10.7 | 0' - 4" | 0' - 0 11/32" | 0' - 0 3/16" |
| HSS5X4X1/8 | 0.01 SF | 0' - 5" | Rect. | 7.3 | 0' - 4" | 0' - 0 7/32" | 0' - 0 1/8" |
| HSS5X3X1/2 | 0.04 SF | 0' - 5" | Rect. | 21.5 | 0' - 3" | 0' - 0 15/16" | 0' - 0 15/32" |
| HSS5X3X3/8 | 0.03 SF | 0' - 5" | Rect. | 17.2 | 0' - 3" | 0' - 0 11/16" | 0' - 0 11/32" |
| HSS5X3X5/16 | 0.03 SF | 0' - 5" | Rect. | 14.8 | 0' - 3" | 0' - 0 19/32" | 0' - 0 9/32" |
| HSS5X3X1/4 | 0.02 SF | 0' - 5" | Rect. | 12.2 | 0' - 3" | 0' - 0 15/32" | 0' - 0 7/32" |
| HSS5X3X3/16 | 0.02 SF | 0' - 5" | Rect. | 9.43 | 0' - 3" | 0' - 0 11/32" | 0' - 0 3/16" |
| HSS5X3X1/8 | 0.01 SF | 0' - 5" | Rect. | 6.45 | 0' - 3" | 0' - 0 7/32" | 0' - 0 1/8" |
| HSS5X2-1/2X1/4 | 0.02 SF | 0' - 5" | Rect. | 11.3 | 0' - 2 1/2" | 0' - 0 15/32" | 0' - 0 7/32" |
| HSS5X2-1/2X3/16 | 0.02 SF | 0' - 5" | Rect. | 8.79 | 0' - 2 1/2" | 0' - 0 11/32" | 0' - 0 3/16" |
| HSS5X2-1/2X1/8 | 0.01 SF | 0' - 5" | Rect. | 6.02 | 0' - 2 1/2" | 0' - 0 7/32" | 0' - 0 1/8" |
| HSS5X2X3/8 | 0.03 SF | 0' - 5" | Rect. | 14.6 | 0' - 2" | 0' - 0 11/16" | 0' - 0 11/32" |
| HSS5X2X5/16 | 0.02 SF | 0' - 5" | Rect. | 12.7 | 0' - 2" | 0' - 0 19/32" | 0' - 0 9/32" |
| HSS5X2X1/4 | 0.02 SF | 0' - 5" | Rect. | 10.5 | 0' - 2" | 0' - 0 15/32" | 0' - 0 7/32" |
| HSS5X2X3/16 | 0.02 SF | 0' - 5" | Rect. | 8.15 | 0' - 2" | 0' - 0 11/32" | 0' - 0 3/16" |
| HSS5X2X1/8 | 0.01 SF | 0' - 5" | Rect. | 5.6 | 0' - 2" | 0' - 0 7/32" | 0' - 0 1/8" |
| HSS4-1/2X4-1/2X1/2 | 0.05 SF | 0' - 4 1/2" | Square | 24.9 | 0' - 4 1/2" | 0' - 0 15/16" | 0' - 0 15/32" |
| HSS4-1/2X4-1/2X3/8 | 0.04 SF | 0' - 4 1/2" | Square | 19.7 | 0' - 4 1/2" | 0' - 0 11/16" | 0' - 0 11/32" |
| HSS4-1/2X4-1/2X5/16 | 0.03 SF | 0' - 4 1/2" | Square | 16.9 | 0' - 4 1/2" | 0' - 0 19/32" | 0' - 0 9/32" |
| HSS4-1/2X4-1/2X1/4 | 0.03 SF | 0' - 4 1/2" | Square | 13.9 | 0' - 4 1/2" | 0' - 0 15/32" | 0' - 0 7/32" |
| HSS4-1/2X4-1/2X3/16 | 0.02 SF | 0' - 4 1/2" | Square | 10.7 | 0' - 4 1/2" | 0' - 0 11/32" | 0' - 0 3/16" |
| HSS4-1/2X4-1/2X1/8 | 0.01 SF | 0' - 4 1/2" | Square | 7.3 | 0' - 4 1/2" | 0' - 0 7/32" | 0' - 0 1/8" |
| HSS4X4X1/2 | 0.04 SF | 0' - 4" | Square | 21.5 | 0' - 4" | 0' - 0 15/16" | 0' - 0 15/32" |
| HSS4X4X3/8 | 0.03 SF | 0' - 4" | Square | 17.2 | 0' - 4" | 0' - 0 11/16" | 0' - 0 11/32" |
| HSS4X4X5/16 | 0.03 SF | 0' - 4" | Square | 14.8 | 0' - 4" | 0' - 0 19/32" | 0' - 0 9/32" |
| HSS4X4X1/4 | 0.02 SF | 0' - 4" | Square | 12.2 | 0' - 4" | 0' - 0 15/32" | 0' - 0 7/32" |
| HSS4X4X3/16 | 0.02 SF | 0' - 4" | Square | 9.4 | 0' - 4" | 0' - 0 11/32" | 0' - 0 3/16" |
| HSS4X4X1/8 | 0.01 SF | 0' - 4" | Square | 6.45 | 0' - 4" | 0' - 0 7/32" | 0' - 0 1/8" |
| HSS4X3X3/8 | 0.03 SF | 0' - 4" | Rect. | 14.6 | 0' - 3" | 0' - 0 11/16" | 0' - 0 11/32" |
| HSS4X3X5/16 | 0.02 SF | 0' - 4" | Rect. | 12.7 | 0' - 3" | 0' - 0 19/32" | 0' - 0 9/32" |
| HSS4X3X1/4 | 0.02 SF | 0' - 4" | Rect. | 10.5 | 0' - 3" | 0' - 0 15/32" | 0' - 0 7/32" |
| HSS4X3X3/16 | 0.02 SF | 0' - 4" | Rect. | 8.15 | 0' - 3" | 0' - 0 11/32" | 0' - 0 3/16" |
| HSS4X3X1/8 | 0.01 SF | 0' - 4" | Rect. | 5.6 | 0' - 3" | 0' - 0 7/32" | 0' - 0 1/8" |
| HSS4X2-1/2X3/8 | 0.03 SF | 0' - 4" | Rect. | 13.4 | 0' - 2 1/2" | 0' - 0 11/16" | 0' - 0 11/32" |
| HSS4X2-1/2X5/16 | 0.02 SF | 0' - 4" | Rect. | 11.6 | 0' - 2 1/2" | 0' - 0 19/32" | 0' - 0 9/32" |
| HSS4X2-1/2X1/4 | 0.02 SF | 0' - 4" | Rect. | 9.63 | 0' - 2 1/2" | 0' - 0 15/32" | 0' - 0 7/32" |
| HSS4X2-1/2X3/16 | 0.01 SF | 0' - 4" | Rect. | 7.51 | 0' - 2 1/2" | 0' - 0 11/32" | 0' - 0 3/16" |
| HSS4X2-1/2X1/8 | 0.01 SF | 0' - 4" | Rect. | 5.17 | 0' - 2 1/2" | 0' - 0 7/32" | 0' - 0 1/8" |
| HSS4X2X3/8 | 0.02 SF | 0' - 4" | Rect. | 12.1 | 0' - 2" | 0' - 0 11/16" | 0' - 0 11/32" |
| HSS4X2X5/16 | 0.02 SF | 0' - 4" | Rect. | 10.5 | 0' - 2" | 0' - 0 19/32" | 0' - 0 9/32" |
| HSS4X2X1/4 | 0.02 SF | 0' - 4" | Rect. | 8.78 | 0' - 2" | 0' - 0 15/32" | 0' - 0 7/32" |
| HSS4X2X3/16 | 0.01 SF | 0' - 4" | Rect. | 6.87 | 0' - 2" | 0' - 0 11/32" | 0' - 0 3/16" |
| HSS4X2X1/8 | 0.01 SF | 0' - 4" | Rect. | 4.75 | 0' - 2" | 0' - 0 7/32" | 0' - 0 1/8" |
| HSS3-1/2X3-1/2X3/8 | 0.03 SF | 0' - 3 1/2" | Square | 14.6 | 0' - 3 1/2" | 0' - 0 11/16" | 0' - 0 11/32" |
| HSS3-1/2X3-1/2X5/16 | 0.02 SF | 0' - 3 1/2" | Square | 12.7 | 0' - 3 1/2" | 0' - 0 19/32" | 0' - 0 9/32" |
| HSS3-1/2X3-1/2X1/4 | 0.02 SF | 0' - 3 1/2" | Square | 10.5 | 0' - 3 1/2" | 0' - 0 15/32" | 0' - 0 7/32" |
| HSS3-1/2X3-1/2X3/16 | 0.02 SF | 0' - 3 1/2" | Square | 8.13 | 0' - 3 1/2" | 0' - 0 11/32" | 0' - 0 3/16" |
| HSS3-1/2X3-1/2X1/8 | 0.01 SF | 0' - 3 1/2" | Square | 5.6 | 0' - 3 1/2" | 0' - 0 7/32" | 0' - 0 1/8" |
| HSS3-1/2X2X1/4 | 0.02 SF | 0' - 3 1/2" | Rect. | 7.93 | 0' - 2" | 0' - 0 15/32" | 0' - 0 7/32" |
| HSS3-1/2X2X3/16 | 0.01 SF | 0' - 3 1/2" | Rect. | 6.23 | 0' - 2" | 0' - 0 11/32" | 0' - 0 3/16" |
| HSS3-1/2X2X1/8 | 0.01 SF | 0' - 3 1/2" | Rect. | 4.32 | 0' - 2" | 0' - 0 7/32" | 0' - 0 1/8" |
| HSS3-1/2X1-1/2X1/4 | 0.01 SF | 0' - 3 1/2" | Rect. | 7.08 | 0' - 1 1/2" | 0' - 0 15/32" | 0' - 0 7/32" |
| HSS3-1/2X1-1/2X3/16 | 0.01 SF | 0' - 3 1/2" | Rect. | 5.59 | 0' - 1 1/2" | 0' - 0 11/32" | 0' - 0 3/16" |
| HSS3-1/2X1-1/2X1/8 | 0.01 SF | 0' - 3 1/2" | Rect. | 3.9 | 0' - 1 1/2" | 0' - 0 7/32" | 0' - 0 1/8" |
| HSS3X3X3/8 | 0.02 SF | 0' - 3" | Square | 12.1 | 0' - 3" | 0' - 0 11/16" | 0' - 0 11/32" |
| HSS3X3X5/16 | 0.02 SF | 0' - 3" | Square | 10.5 | 0' - 3" | 0' - 0 19/32" | 0' - 0 9/32" |
| HSS3X3X1/4 | 0.02 SF | 0' - 3" | Square | 8.78 | 0' - 3" | 0' - 0 15/32" | 0' - 0 7/32" |
| HSS3X3X3/16 | 0.01 SF | 0' - 3" | Square | 6.85 | 0' - 3" | 0' - 0 11/32" | 0' - 0 3/16" |
| HSS3X3X1/8 | 0.01 SF | 0' - 3" | Square | 4.75 | 0' - 3" | 0' - 0 7/32" | 0' - 0 1/8" |
| HSS3X2-1/2X5/16 | 0.02 SF | 0' - 3" | Rect. | 9.47 | 0' - 2 1/2" | 0' - 0 19/32" | 0' - 0 9/32" |
| HSS3X2-1/2X1/4 | 0.02 SF | 0' - 3" | Rect. | 7.93 | 0' - 2 1/2" | 0' - 0 15/32" | 0' - 0 7/32" |
| HSS3X2-1/2X3/16 | 0.01 SF | 0' - 3" | Rect. | 6.23 | 0' - 2 1/2" | 0' - 0 11/32" | 0' - 0 3/16" |
| HSS3X2-1/2X1/8 | 0.01 SF | 0' - 3" | Rect. | 4.32 | 0' - 2 1/2" | 0' - 0 7/32" | 0' - 0 1/8" |
| HSS3X2X5/16 | 0.02 SF | 0' - 3" | Rect. | 8.41 | 0' - 2" | 0' - 0 19/32" | 0' - 0 9/32" |
| HSS3X2X1/4 | 0.01 SF | 0' - 3" | Rect. | 7.08 | 0' - 2" | 0' - 0 15/32" | 0' - 0 7/32" |
| HSS3X2X3/16 | 0.01 SF | 0' - 3" | Rect. | 5.59 | 0' - 2" | 0' - 0 11/32" | 0' - 0 3/16" |
| HSS3X2X1/8 | 0.01 SF | 0' - 3" | Rect. | 3.9 | 0' - 2" | 0' - 0 7/32" | 0' - 0 1/8" |
| HSS3X1-1/2X1/4 | 0.01 SF | 0' - 3" | Rect. | 6.23 | 0' - 1 1/2" | 0' - 0 15/32" | 0' - 0 7/32" |
| HSS3X1-1/2X3/16 | 0.01 SF | 0' - 3" | Rect. | 4.95 | 0' - 1 1/2" | 0' - 0 11/32" | 0' - 0 3/16" |
| HSS3X1-1/2X1/8 | 0.01 SF | 0' - 3" | Rect. | 3.47 | 0' - 1 1/2" | 0' - 0 7/32" | 0' - 0 1/8" |
| HSS3X1X3/16 | 0.01 SF | 0' - 3" | Rect. | 4.31 | 0' - 1" | 0' - 0 11/32" | 0' - 0 3/16" |
| HSS3X1X1/8 | 0.01 SF | 0' - 3" | Rect. | 3.04 | 0' - 1" | 0' - 0 7/32" | 0' - 0 1/8" |
| HSS2-1/2X2-1/2X5/16 | 0.02 SF | 0' - 2 1/2" | Square | 8.4 | 0' - 2 1/2" | 0' - 0 19/32" | 0' - 0 9/32" |
| HSS2-1/2X2-1/2X1/4 | 0.01 SF | 0' - 2 1/2" | Square | 7.08 | 0' - 2 1/2" | 0' - 0 15/32" | 0' - 0 7/32" |
| HSS2-1/2X2-1/2X3/16 | 0.01 SF | 0' - 2 1/2" | Square | 5.57 | 0' - 2 1/2" | 0' - 0 11/32" | 0' - 0 3/16" |
| HSS2-1/2X2-1/2X1/8 | 0.01 SF | 0' - 2 1/2" | Square | 3.9 | 0' - 2 1/2" | 0' - 0 7/32" | 0' - 0 1/8" |
| HSS2-1/2X2X1/4 | 0.01 SF | 0' - 2 1/2" | Rect. | 6.23 | 0' - 2" | 0' - 0 15/32" | 0' - 0 7/32" |
| HSS2-1/2X2X3/16 | 0.01 SF | 0' - 2 1/2" | Rect. | 4.95 | 0' - 2" | 0' - 0 11/32" | 0' - 0 3/16" |
| HSS2-1/2X2X1/8 | 0.01 SF | 0' - 2 1/2" | Rect. | 3.47 | 0' - 2" | 0' - 0 7/32" | 0' - 0 1/8" |
| HSS2-1/2X1-1/2X1/4 | 0.01 SF | 0' - 2 1/2" | Rect. | 5.38 | 0' - 1 1/2" | 0' - 0 15/32" | 0' - 0 7/32" |
| HSS2-1/2X1-1/2X3/16 | 0.01 SF | 0' - 2 1/2" | Rect. | 4.31 | 0' - 1 1/2" | 0' - 0 11/32" | 0' - 0 3/16" |
| HSS2-1/2X1-1/2X1/8 | 0.01 SF | 0' - 2 1/2" | Rect. | 3.04 | 0' - 1 1/2" | 0' - 0 7/32" | 0' - 0 1/8" |
| HSS2-1/2X1X3/16 | 0.01 SF | 0' - 2 1/2" | Rect. | 3.67 | 0' - 1" | 0' - 0 11/32" | 0' - 0 3/16" |
| HSS2-1/2X1X1/8 | 0.01 SF | 0' - 2 1/2" | Rect. | 2.62 | 0' - 1" | 0' - 0 7/32" | 0' - 0 1/8" |
| HSS2-1/4X2-1/4X1/4 | 0.01 SF | 0' - 2 1/4" | Rect. | 6.23 | 0' - 2 1/4" | 0' - 0 15/32" | 0' - 0 7/32" |
| HSS2-1/4X2-1/4X3/16 | 0.01 SF | 0' - 2 1/4" | Rect. | 4.94 | 0' - 2 1/4" | 0' - 0 11/32" | 0' - 0 3/16" |
| HSS2-1/4X2-1/4X1/8 | 0.01 SF | 0' - 2 1/4" | Rect. | 3.47 | 0' - 2 1/4" | 0' - 0 7/32" | 0' - 0 1/8" |
| HSS2-1/4X2X3/16 | 0.01 SF | 0' - 2 1/4" | Rect. | 4.63 | 0' - 2 1/4" | 0' - 0 11/32" | 0' - 0 3/16" |
| HSS2-1/4X2X1/8 | 0.01 SF | 0' - 2 1/4" | Rect. | 3.26 | 0' - 2 1/4" | 0' - 0 7/32" | 0' - 0 1/8" |
| HSS2X2X1/4 | 0.01 SF | 0' - 2" | Square | 5.38 | 0' - 2" | 0' - 0 15/32" | 0' - 0 7/32" |
| HSS2X2X3/16 | 0.01 SF | 0' - 2" | Square | 4.3 | 0' - 2" | 0' - 0 11/32" | 0' - 0 3/16" |
| HSS2X2X1/8 | 0.01 SF | 0' - 2" | Square | 3.04 | 0' - 2" | 0' - 0 7/32" | 0' - 0 1/8" |
| HSS2X1-1/2X3/16 | 0.01 SF | 0' - 2" | Rect. | 3.67 | 0' - 1 1/2" | 0' - 0 11/32" | 0' - 0 3/16" |
| HSS2X1-1/2X1/8 | 0.01 SF | 0' - 2" | Rect. | 2.62 | 0' - 1 1/2" | 0' - 0 7/32" | 0' - 0 1/8" |
| HSS2X1X3/16 | 0.01 SF | 0' - 2" | Rect. | 3.03 | 0' - 1" | 0' - 0 11/32" | 0' - 0 3/16" |
| HSS2X1X1/8 | 0 SF | 0' - 2" | Rect. | 2.19 | 0' - 1" | 0' - 0 7/32" | 0' - 0 1/8" |
| HSS1-3/4X1-3/4X3/16 - Obsolete | 0.01 SF | 0' - 1 3/4" | Square | 3.66 | 0' - 1 3/4" | 0' - 0 11/32" | 0' - 0 3/16" |
| HSS1-5/8X1-5/8X3/16 - Obsolete | 0.01 SF | 0' - 1 5/8" | Square | 3.34 | 0' - 1 5/8" | 0' - 0 11/32" | 0' - 0 3/16" |
| HSS1-5/8X1-5/8X1/8 - Obsolete | 0 SF | 0' - 1 5/8" | Square | 2.41 | 0' - 1 5/8" | 0' - 0 7/32" | 0' - 0 1/8" |
| HSS1-1/2X1-1/2X3/16 - Obsolete | 0.01 SF | 0' - 1 1/2" | Square | 3.02 | 0' - 1 1/2" | 0' - 0 11/32" | 0' - 0 3/16" |
| HSS1-1/2X1-1/2X1/8 - Obsolete | 0 SF | 0' - 1 1/2" | Square | 2.19 | 0' - 1 1/2" | 0' - 0 7/32" | 0' - 0 1/8" |
| HSS1-1/4X1-1/4X3/16 - Obsolete | 0 SF | 0' - 1 1/4" | Square | 2.38 | 0' - 1 1/4" | 0' - 0 11/32" | 0' - 0 3/16" |
| HSS1-1/4X1-1/4X1/8 - Obsolete | 0 SF | 0' - 1 1/4" | Square | 1.77 | 0' - 1 1/4" | 0' - 0 7/32" | 0' - 0 1/8" |
